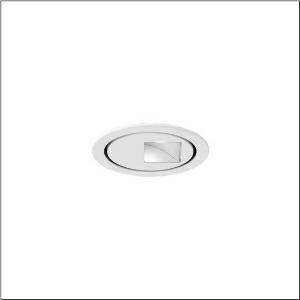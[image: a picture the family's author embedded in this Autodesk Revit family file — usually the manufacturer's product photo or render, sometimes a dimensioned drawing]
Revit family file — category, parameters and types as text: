
# Revit family: lunis_11_micro_round_51dj11b71wg21
name_source: partatom
category: Lighting Fixtures
units: mm (PartAtom-declared; Revit-internal decimal feet)

## family parameters
Cut with Voids When Loaded = No
Host = Face
Light Source = No
Part Type = Normal
Room Calculation Point = No
Round Connector Dimension = Use Diameter
Shared = No

## types (1)
- Lunis 11 micro round (1 x LED 4000K / CRI = 80 (unbekannt), 1400 lm, 4000K)
    Apparent Load = 20 VA
    CIE Flux Codes = 42 75 96 100 100
    Color Rendering = 80
    Color Temperature = 4000K
    Default Elevation = 1800 mm
    Description = Lunis 11 micro round, downlight, light control with wallwasher, of highly reflective aluminium, highly specular, light emission: direct distribution, LED rated luminous flux: 1.400lm, light colour: 840, with terminal, 3-pole, mains connection: 220..230V, AC, 50/60Hz, LED module, of aluminium, highly specular, white, diameter: 114mm, clamping range: 1..40mm, recessing ring, of plastic, traffic white (RAL 9016), protection rating (complete): IP20, insulation class (complete): insulation class II (safety insulation), certification: CE, permissible ambient temperature for indoor applications: 0..+35°C, packaging unit: 1 piece
    Height = 0 mm  [stored 0 ft]
    Lamp = 1 x LED 4000K / CRI >= 80 (unbekannt)
    Lamp Light Flux = 1400 lm
    Lamp count = 1
    Length = 114 mm
    Luminous efficacy = 71 lm/W
    Manufacturer = Siteco
    ModVariant = No
    Model = 51DJ11B71WG21
    Mounting Place = Ceiling
    Mounting Type = Recessed
    Number of Poles = 1
    OnlyDefault = Yes
    Power Factor = 1
    Product Name = Lunis 11 micro round
    Product group = downlight
    ProductGroupID = 400
    Protection Class = Protection class II
    Protection Degree = IP 20
    RLX_Detail_Level = 1
    RLX_Emergency_Light_Flux = 0 lm
    RLX_Emergency_Type = 0
    RLX_Emergency_Type_DB = No
    RlxData = <blob elided: 41049 chars, md5=bdfce9d4>
    Socket = socket
    Standby Power = 0 W
    System Light Flux = 1400 lm
    System Power = 20 W
    Type Comments = Product without accessories
    Type Image = l_1004773.jpg
    URL = http://relux.com
    VarID = ---
    Voltage = 0 V
    Weight = 0.00 kg
    Width = 114 mm

note: [stored X ft] marks values corroborated as IEEE doubles in the binary element streams (Revit-internal decimal feet)

## geometry (parser evidence)
native form markers: Blend x4, Sweep x11
no freeform markers — native parametric forms only
